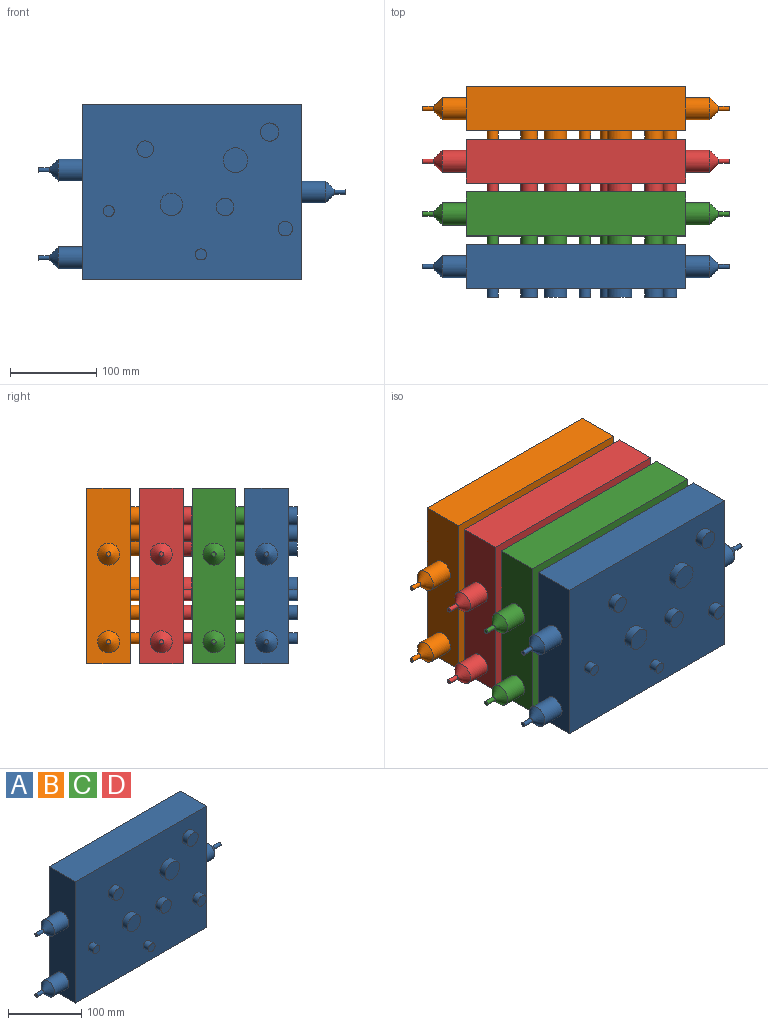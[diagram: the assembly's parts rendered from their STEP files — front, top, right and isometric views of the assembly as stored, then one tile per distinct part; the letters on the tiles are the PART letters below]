
ASSEMBLY  parts=4 mates=9
PART A: 34 faces, bbox 355.6x61x203.2 mm
  f0: plane 203.2x50.8mm, normal (-1,0,0), area 9309.1mm2, adj f1,f3,f4,f5,f23,f24
  f1: plane 254x203.2mm, normal (0,-1,0), area 49007.9mm2, adj f0,f2,f4,f5,f6,f8,f10,f12
  f2: plane 203.2x50.8mm, normal (1,0,0), area 9815.9mm2, adj f1,f3,f4,f5,f22
  f3: plane 254x203.2mm, normal (0,1,0), area 51612.8mm2, adj f0,f2,f4,f5
  f4: plane 254x50.8mm, normal (0,0,1), area 12903.2mm2, adj f0,f1,f2,f3
  f5: plane 254x50.8mm, normal (0,0,-1), area 12903.2mm2, adj f0,f1,f2,f3
  f6: cylinder r=9.63mm len=19.27mm, axis (0,1,0), area 615mm2, adj f1,f7
  f7: plane 19.27x19.27mm, normal (0,-1,0), area 291.6mm2, adj f6
  f8: cylinder r=14.2mm len=28.4mm, axis (0,1,0), area 906.4mm2, adj f1,f9
  f9: plane 28.4x28.4mm, normal (0,-1,0), area 633.3mm2, adj f8
  f10: cylinder r=12.97mm len=25.94mm, axis (0,1,0), area 828.1mm2, adj f1,f11
  f11: plane 25.94x25.94mm, normal (0,-1,0), area 528.6mm2, adj f10
  f12: cylinder r=8.37mm len=16.73mm, axis (0,1,0), area 534mm2, adj f1,f13
  f13: plane 16.73x16.73mm, normal (0,-1,0), area 219.8mm2, adj f12
  f14: cylinder r=6.44mm len=12.87mm, axis (0,1,0), area 410.9mm2, adj f1,f15
  f15: plane 12.87x12.87mm, normal (0,-1,0), area 130.2mm2, adj f14
  f16: cylinder r=6.41mm len=12.83mm, axis (0,1,0), area 409.4mm2, adj f1,f17
  f17: plane 12.83x12.83mm, normal (0,-1,0), area 129.2mm2, adj f16
  f18: cylinder r=10.12mm len=20.24mm, axis (0,1,0), area 646mm2, adj f1,f19
  f19: plane 20.24x20.24mm, normal (0,-1,0), area 321.7mm2, adj f18
  f20: cylinder r=10.56mm len=21.13mm, axis (0,1,0), area 674.3mm2, adj f1,f21
  f21: plane 21.13x21.13mm, normal (0,-1,0), area 350.5mm2, adj f20
  f22: cylinder r=12.7mm len=27.94mm, axis (-1,0,0), area 2229.5mm2, adj f2,f27
  f23: cylinder r=12.7mm len=27.94mm, axis (1,0,0), area 2229.5mm2, adj f0,f29
  f24: cylinder r=12.7mm len=27.94mm, axis (1,0,0), area 2229.5mm2, adj f0,f28
  f25: cylinder r=2.54mm len=12.7mm, axis (-1,0,0), area 202.7mm2, adj f26,f27
  f26: plane 5.08x5.08mm, normal (1,0,0), area 20.3mm2, adj f25
  f27: cone r=2.54mm half-angle=45deg, axis (-1,0,0), area 687.9mm2, adj f22,f25
  f28: cone r=2.54mm half-angle=45deg, axis (1,0,0), area 687.9mm2, adj f24,f32
  f29: cone r=2.54mm half-angle=45deg, axis (1,0,0), area 687.9mm2, adj f23,f30
  f30: cylinder r=2.54mm len=12.7mm, axis (1,0,0), area 202.7mm2, adj f29,f31
  f31: plane 5.08x5.08mm, normal (-1,0,0), area 20.3mm2, adj f30
  f32: cylinder r=2.54mm len=12.7mm, axis (1,0,0), area 202.7mm2, adj f28,f33
  f33: plane 5.08x5.08mm, normal (-1,0,0), area 20.3mm2, adj f32
PART B: same geometry as A
PART C: same geometry as A
PART D: same geometry as A
PLACE A t=(390.53,320.09,97.97)mm
PLACE B t=(390.53,502.97,97.97)mm
PLACE C t=(390.53,381.05,97.97)mm
PLACE D t=(390.53,442.01,97.97)mm
MATE planar A.f5 <-> C.f5  axis (0,0,-1) through (517.53,345.49,97.97)mm
MATE planar D.f10 <-> C.f3  axis (0,-1,0) through (493.66,431.85,185.35)mm
MATE planar C.f22 <-> D.f2  axis (1,0,0) through (644.53,406.45,199.57)mm
MATE planar B.f5 <-> D.f5  axis (0,0,-1) through (517.53,528.37,97.97)mm
MATE planar A.f2 <-> C.f22  axis (1,0,0) through (644.53,345.49,301.17)mm
MATE planar D.f22 <-> B.f22  axis (1,0,0) through (644.53,467.41,199.57)mm
MATE planar D.f5 <-> C.f5  axis (0,0,-1) through (517.53,467.41,97.97)mm
MATE planar B.f10 <-> D.f3  axis (0,-1,0) through (493.66,492.81,185.35)mm
MATE planar C.f10 <-> A.f3  axis (0,-1,0) through (493.66,370.89,185.35)mm
